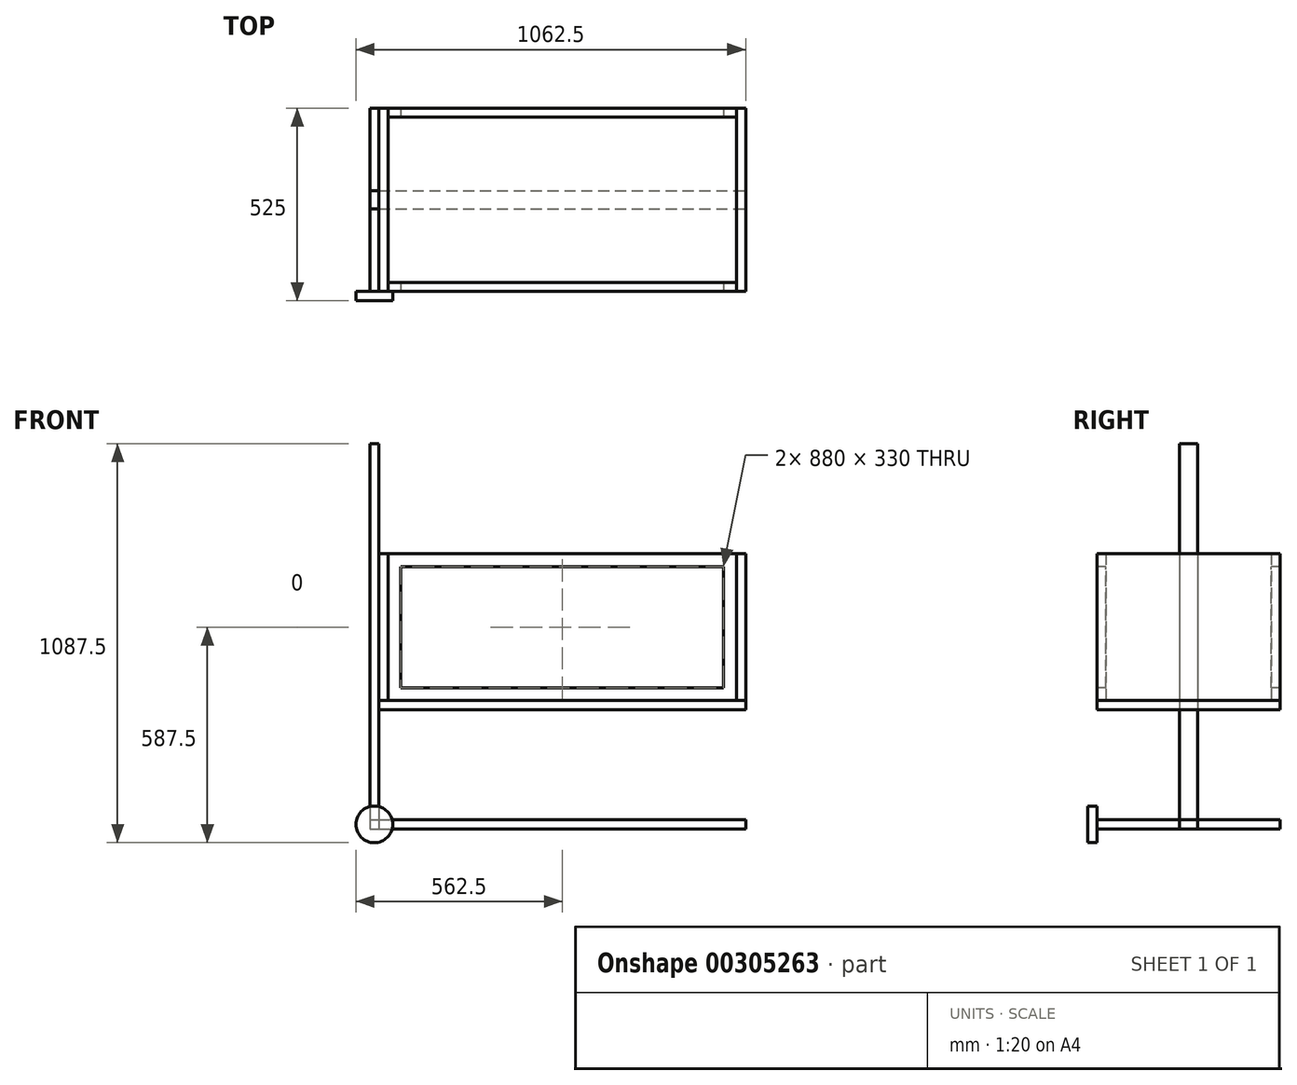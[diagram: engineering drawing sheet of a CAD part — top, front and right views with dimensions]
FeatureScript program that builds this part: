
annotation { "Feature Type Name" : "Feature", "Feature Type Description" : "" }
export const myFeature = defineFeature(function(context is Context, id is Id, definition is map)
    precondition{}
    {
        {
            var Q0;
            Q0=qCreatedBy(makeId("Top.planeOp"),FACE);
            var sketch = newSketch(context, id + "F0", { "sketchPlane" : qUnion([Q0])});
            skLineSegment(sketch, "E0.bottom", {"start": v(-500, 250) * mm, "end": v(500, 250) * mm});
            skLineSegment(sketch, "E0.top", {"start": v(-500, -250) * mm, "end": v(500, -250) * mm});
            skLineSegment(sketch, "E0.left", {"start": v(-500, 250) * mm, "end": v(-500, -250) * mm});
            skLineSegment(sketch, "E0.right", {"start": v(500, 250) * mm, "end": v(500, -250) * mm});
            skSolve(sketch);
        }
        {
            var Q0;
            Q0 = qSketchRegion(id + "F0", true);
            extrude(context, id + "F1", {"entities" : qUnion([Q0]), "depth" : 25 * mm});
        }
        {
            var Q0;
            Q0=makeQuery(id+"F1.opExtrude","CAP_FACE",FACE,{"disambiguationData":[OSD([sQuery(id+"F0.wireOp",EDGE,"E0.bottom"),sQuery(id+"F0.wireOp",EDGE,"E0.top"),sQuery(id+"F0.wireOp",EDGE,"E0.left"),sQuery(id+"F0.wireOp",EDGE,"E0.right")])],"isStart":false});
            var sketch = newSketch(context, id + "F2", { "sketchPlane" : qUnion([Q0])});
            skLineSegment(sketch, "E1.bottom", {"start": v(-500, 250) * mm, "end": v(-475, 250) * mm});
            skLineSegment(sketch, "E1.top", {"start": v(-500, -250) * mm, "end": v(-475, -250) * mm});
            skLineSegment(sketch, "E1.left", {"start": v(-500, 250) * mm, "end": v(-500, -250) * mm});
            skLineSegment(sketch, "E1.right", {"start": v(-475, 250) * mm, "end": v(-475, -250) * mm});
            skSolve(sketch);
        }
        {
            var Q0;
            Q0 = qSketchRegion(id + "F2", true);
            extrude(context, id + "F3", {"entities" : qUnion([Q0]), "depth" : 400 * mm});
        }
        {
            var Q0;
            Q0=makeQuery(id+"F1.opExtrude","CAP_FACE",FACE,{"disambiguationData":[OSD([sQuery(id+"F0.wireOp",EDGE,"E0.bottom"),sQuery(id+"F0.wireOp",EDGE,"E0.top"),sQuery(id+"F0.wireOp",EDGE,"E0.left"),sQuery(id+"F0.wireOp",EDGE,"E0.right")])],"isStart":false});
            var sketch = newSketch(context, id + "F4", { "sketchPlane" : qUnion([Q0])});
            skLineSegment(sketch, "E2.bottom", {"start": v(500, 250) * mm, "end": v(475, 250) * mm});
            skLineSegment(sketch, "E2.top", {"start": v(500, -250) * mm, "end": v(475, -250) * mm});
            skLineSegment(sketch, "E2.left", {"start": v(500, 250) * mm, "end": v(500, -250) * mm});
            skLineSegment(sketch, "E2.right", {"start": v(475, 250) * mm, "end": v(475, -250) * mm});
            skSolve(sketch);
        }
        {
            var Q0;
            Q0 = qSketchRegion(id + "F4", true);
            var Q1;
            Q1=makeQuery(id+"F3.opExtrude","CAP_FACE",FACE,{"disambiguationData":[OSD([sQuery(id+"F2.wireOp",EDGE,"E1.bottom"),sQuery(id+"F2.wireOp",EDGE,"E1.top"),sQuery(id+"F2.wireOp",EDGE,"E1.left"),sQuery(id+"F2.wireOp",EDGE,"E1.right")])],"isStart":false});
            extrude(context, id + "F5", {"entities" : qUnion([Q0]), "endBound" : BoundingType.UP_TO_SURFACE, "endBoundEntityFace" : qUnion([Q1]), "depth" : 500 * mm});
        }
        {
            var Q0;
            Q0=makeQuery(id+"F1.opExtrude","CAP_FACE",FACE,{"disambiguationData":[OSD([sQuery(id+"F0.wireOp",EDGE,"E0.bottom"),sQuery(id+"F0.wireOp",EDGE,"E0.top"),sQuery(id+"F0.wireOp",EDGE,"E0.left"),sQuery(id+"F0.wireOp",EDGE,"E0.right")])],"isStart":false});
            var sketch = newSketch(context, id + "F6", { "sketchPlane" : qUnion([Q0])});
            skLineSegment(sketch, "E3.bottom", {"start": v(-475, 250) * mm, "end": v(475, 250) * mm});
            skLineSegment(sketch, "E3.top", {"start": v(-475, 225) * mm, "end": v(475, 225) * mm});
            skLineSegment(sketch, "E3.left", {"start": v(-475, 250) * mm, "end": v(-475, 225) * mm});
            skLineSegment(sketch, "E3.right", {"start": v(475, 250) * mm, "end": v(475, 225) * mm});
            skSolve(sketch);
        }
        {
            var Q0;
            Q0 = qSketchRegion(id + "F6", true);
            var Q1;
            Q1=makeQuery(id+"F3.opExtrude","CAP_FACE",FACE,{"disambiguationData":[OSD([sQuery(id+"F2.wireOp",EDGE,"E1.bottom"),sQuery(id+"F2.wireOp",EDGE,"E1.top"),sQuery(id+"F2.wireOp",EDGE,"E1.left"),sQuery(id+"F2.wireOp",EDGE,"E1.right")])],"isStart":false});
            extrude(context, id + "F7", {"entities" : qUnion([Q0]), "endBound" : BoundingType.UP_TO_SURFACE, "endBoundEntityFace" : qUnion([Q1]), "depth" : 25 * mm});
        }
        {
            var Q0;
            Q0=makeQuery(id+"F1.opExtrude","CAP_FACE",FACE,{"disambiguationData":[OSD([sQuery(id+"F0.wireOp",EDGE,"E0.bottom"),sQuery(id+"F0.wireOp",EDGE,"E0.top"),sQuery(id+"F0.wireOp",EDGE,"E0.left"),sQuery(id+"F0.wireOp",EDGE,"E0.right")])],"isStart":false});
            var sketch = newSketch(context, id + "F8", { "sketchPlane" : qUnion([Q0])});
            skLineSegment(sketch, "E4.bottom", {"start": v(-475, -250) * mm, "end": v(475, -250) * mm});
            skLineSegment(sketch, "E4.top", {"start": v(-475, -225) * mm, "end": v(475, -225) * mm});
            skLineSegment(sketch, "E4.left", {"start": v(-475, -250) * mm, "end": v(-475, -225) * mm});
            skLineSegment(sketch, "E4.right", {"start": v(475, -250) * mm, "end": v(475, -225) * mm});
            skSolve(sketch);
        }
        {
            var Q0;
            Q0 = qSketchRegion(id + "F8", true);
            var Q1;
            Q1=makeQuery(id+"F3.opExtrude","CAP_FACE",FACE,{"disambiguationData":[OSD([sQuery(id+"F2.wireOp",EDGE,"E1.bottom"),sQuery(id+"F2.wireOp",EDGE,"E1.top"),sQuery(id+"F2.wireOp",EDGE,"E1.left"),sQuery(id+"F2.wireOp",EDGE,"E1.right")])],"isStart":false});
            extrude(context, id + "F9", {"entities" : qUnion([Q0]), "endBound" : BoundingType.UP_TO_SURFACE, "endBoundEntityFace" : qUnion([Q1]), "depth" : 25 * mm});
        }
        {
            var Q0;
            Q0=makeQuery(id+"F5.opExtrude","SWEPT_FACE",FACE,{"disambiguationData":[OSD([sQuery(id+"F4.wireOp",EDGE,"E2.left")])]});
            var sketch = newSketch(context, id + "F10", { "sketchPlane" : qUnion([Q0])});
            skLineSegment(sketch, "E5.bottom", {"start": v(-25, 725) * mm, "end": v(25, 725) * mm});
            skLineSegment(sketch, "E5.top", {"start": v(-25, -300) * mm, "end": v(25, -300) * mm});
            skLineSegment(sketch, "E5.left", {"start": v(-25, 725) * mm, "end": v(-25, -300) * mm});
            skLineSegment(sketch, "E5.right", {"start": v(25, 725) * mm, "end": v(25, -300) * mm});
            skSolve(sketch);
        }
        {
            var Q0;
            Q0 = qSketchRegion(id + "F10", true);
            extrude(context, id + "F11", {"entities" : qUnion([Q0]), "depth" : 25 * mm});
        }
        {
            var Q0;
            Q0=makeQuery(id+"F3.opExtrude","SWEPT_FACE",FACE,{"disambiguationData":[OSD([sQuery(id+"F2.wireOp",EDGE,"E1.left")])]});
            var sketch = newSketch(context, id + "F12", { "sketchPlane" : qUnion([Q0])});
            skLineSegment(sketch, "E6.bottom", {"start": v(-25, 725) * mm, "end": v(25, 725) * mm});
            skLineSegment(sketch, "E6.top", {"start": v(-25, -300) * mm, "end": v(25, -300) * mm});
            skLineSegment(sketch, "E6.left", {"start": v(-25, 725) * mm, "end": v(-25, -300) * mm});
            skLineSegment(sketch, "E6.right", {"start": v(25, 725) * mm, "end": v(25, -300) * mm});
            skSolve(sketch);
        }
        {
            var Q0;
            Q0 = qSketchRegion(id + "F12", true);
            extrude(context, id + "F13", {"entities" : qUnion([Q0]), "depth" : 25 * mm});
        }
        {
            var Q0;
            Q0=makeQuery(id+"F13.opExtrude","SWEPT_FACE",FACE,{"disambiguationData":[OSD([sQuery(id+"F12.wireOp",EDGE,"E6.top")])]});
            var sketch = newSketch(context, id + "F14", { "sketchPlane" : qUnion([Q0])});
            skLineSegment(sketch, "E7.bottom", {"start": v(-500, 25) * mm, "end": v(500, 25) * mm});
            skLineSegment(sketch, "E7.top", {"start": v(-500, -25) * mm, "end": v(500, -25) * mm});
            skLineSegment(sketch, "E7.left", {"start": v(-500, 25) * mm, "end": v(-500, -25) * mm});
            skLineSegment(sketch, "E7.right", {"start": v(500, 25) * mm, "end": v(500, -25) * mm});
            skSolve(sketch);
        }
        {
            var Q0;
            Q0 = qSketchRegion(id + "F14", true);
            extrude(context, id + "F15", {"entities" : qUnion([Q0]), "depth" : 25 * mm});
        }
        {
            var Q0;
            Q0=qCreatedBy(makeId("Front.planeOp"),FACE);
            var sketch = newSketch(context, id + "F16", { "sketchPlane" : qUnion([Q0])});
            skLineSegment(sketch, "E8.bottom", {"start": v(-525, -300) * mm, "end": v(-500, -300) * mm});
            skLineSegment(sketch, "E8.top", {"start": v(-525, -325) * mm, "end": v(-500, -325) * mm});
            skLineSegment(sketch, "E8.left", {"start": v(-525, -300) * mm, "end": v(-525, -325) * mm});
            skLineSegment(sketch, "E8.right", {"start": v(-500, -300) * mm, "end": v(-500, -325) * mm});
            skSolve(sketch);
        }
        {
            var Q0;
            Q0 = qSketchRegion(id + "F16", true);
            extrude(context, id + "F17", {"entities" : qUnion([Q0]), "depth" : 250 * mm, "hasSecondDirection" : true, "secondDirectionOppositeDirection" : true, "secondDirectionDepth" : 250 * mm});
        }
        {
            var Q0;
            Q0=makeQuery(id+"F17.opExtrude","CAP_FACE",FACE,{"disambiguationData":[OSD([sQuery(id+"F16.wireOp",EDGE,"E8.bottom"),sQuery(id+"F16.wireOp",EDGE,"E8.top"),sQuery(id+"F16.wireOp",EDGE,"E8.left"),sQuery(id+"F16.wireOp",EDGE,"E8.right")])],"isStart":false});
            var sketch = newSketch(context, id + "F18", { "sketchPlane" : qUnion([Q0])});
            skCircle(sketch, "E9", {"center": v(-512.5, -312.5) * mm, "radius": 50 * mm});
            skPoint(sketch, "E9.centerSnap0", {"position": v(-512.5, -325) * mm});
            skPoint(sketch, "E9.centerSnap1", {"position": v(-500, -312.5) * mm});
            skSolve(sketch);
        }
        {
            var Q0;
            Q0 = qSketchRegion(id + "F18", true);
            extrude(context, id + "F19", {"entities" : qUnion([Q0]), "depth" : 25 * mm});
        }
        {
            var Q0;
            Q0=makeQuery(id+"F11.opExtrude","SWEPT_BODY",BODY,{"disambiguationData":[OSD([sQuery(id+"F10.wireOp",EDGE,"E5.bottom"),sQuery(id+"F10.wireOp",EDGE,"E5.top"),sQuery(id+"F10.wireOp",EDGE,"E5.left"),sQuery(id+"F10.wireOp",EDGE,"E5.right")])]});
            deleteBodies(context, id + "F20", {"entities" : qUnion([Q0])});
        }
        {
            var Q0;
            Q0=makeQuery(id+"F9.opExtrude","SWEPT_FACE",FACE,{"disambiguationData":[OSD([sQuery(id+"F8.wireOp",EDGE,"E4.bottom")])]});
            var sketch = newSketch(context, id + "F21", { "sketchPlane" : qUnion([Q0])});
            skLineSegment(sketch, "E10.bottom", {"start": v(-440, 390) * mm, "end": v(440, 390) * mm});
            skLineSegment(sketch, "E10.top", {"start": v(-440, 60) * mm, "end": v(440, 60) * mm});
            skLineSegment(sketch, "E10.left", {"start": v(-440, 390) * mm, "end": v(-440, 60) * mm});
            skLineSegment(sketch, "E10.right", {"start": v(440, 390) * mm, "end": v(440, 60) * mm});
            skSolve(sketch);
        }
        {
            var Q0;
            Q0=makeQuery(id+"F21.imprint","IMPRINT",FACE,{"disambiguationData":[TD([[makeQuery(id+"F21.imprint","IMPRINT",EDGE,{"derivedFrom":sQuery(id+"F21.wireOp",EDGE,"E10.bottom")}),-1.0]])]});
            extrude(context, id + "F22", {"entities" : qUnion([Q0]), "operationType" : NewBodyOperationType.REMOVE, "endBound" : BoundingType.THROUGH_ALL, "oppositeDirection" : true, "depth" : 25 * mm});
        }
        {
            var Q0;
            Q0=makeQuery(id+"F22.boolean.opBoolean","COPY",FACE,{"derivedFrom":makeQuery(id+"F22.opExtrude","SWEPT_FACE",FACE,{"disambiguationData":[OSD([sQuery(id+"F21.wireOp",EDGE,"E10.top")])]})});
            var sketch = newSketch(context, id + "F23", { "sketchPlane" : qUnion([Q0])});
            skCircle(sketch, "E11", {"center": v(-402.24, -237.5) * mm, "radius": 12.42 * mm});
            skPoint(sketch, "E11.centerSnap0", {"position": v(-440, -237.5) * mm});
            skSolve(sketch);
        }
        {
            var Q0;
            Q0=sQuery(id+"F23.wireOp",EDGE,"E11");
            extrude(context, id + "F24", {"bodyType" : ToolBodyType.SURFACE, "surfaceEntities" : qUnion([Q0]), "endBound" : BoundingType.UP_TO_NEXT, "depth" : 25 * mm, "offsetDistance" : 25 * mm});
        }
    });
